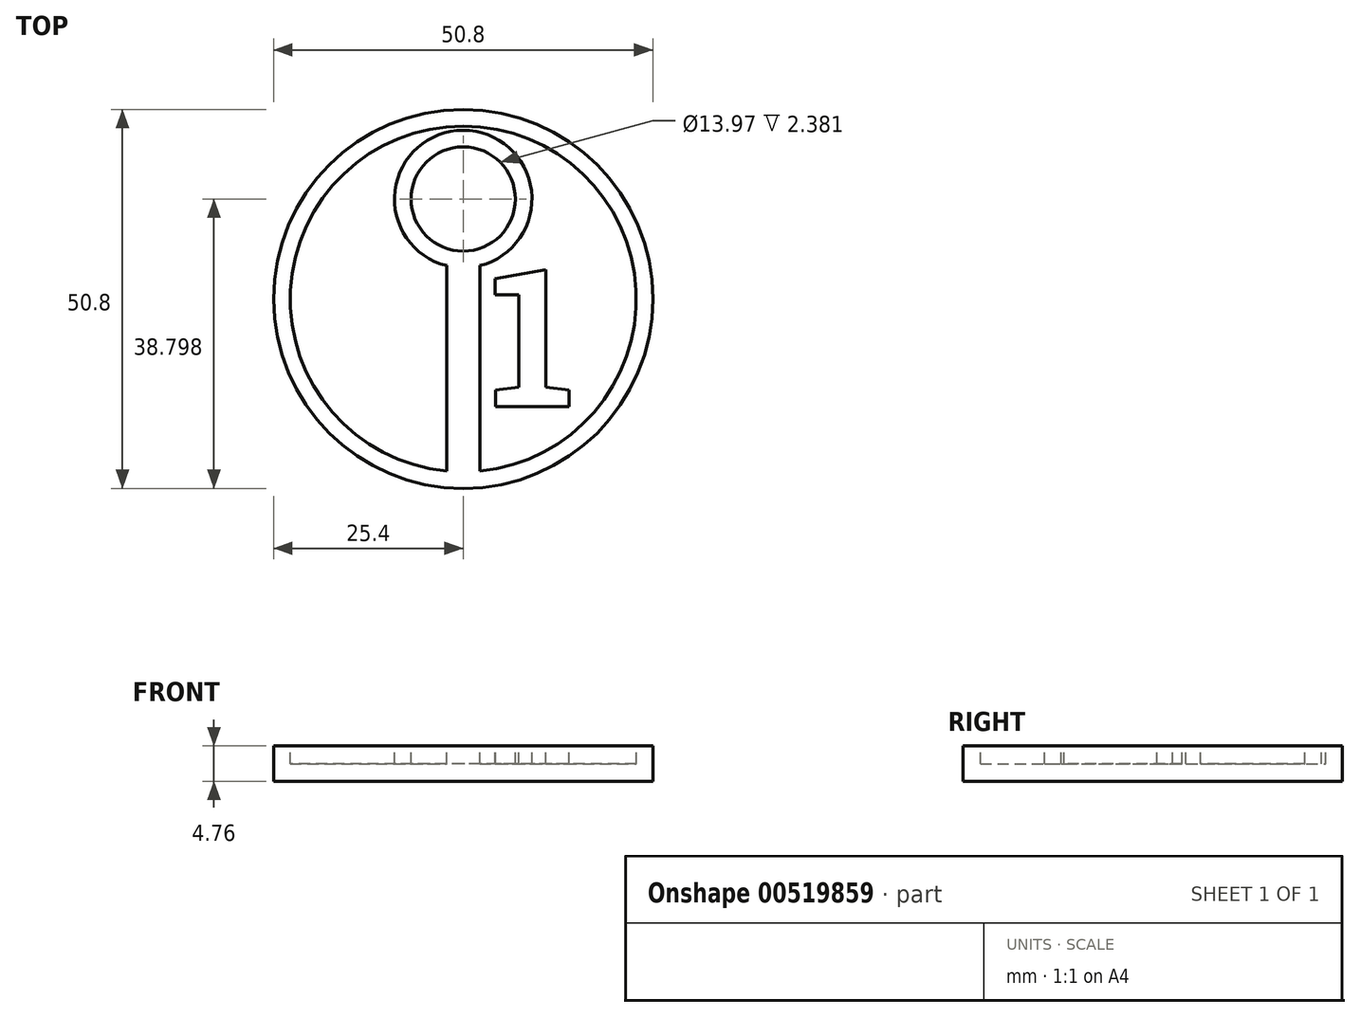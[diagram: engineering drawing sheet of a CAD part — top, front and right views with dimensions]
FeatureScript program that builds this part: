
annotation { "Feature Type Name" : "Feature", "Feature Type Description" : "" }
export const myFeature = defineFeature(function(context is Context, id is Id, definition is map)
    precondition{}
    {
        {
            var Q0;
            Q0=qCreatedBy(makeId("Top.planeOp"),FACE);
            var sketch = newSketch(context, id + "F0", { "sketchPlane" : qUnion([Q0])});
            skCircle(sketch, "E0", {"center": v(0, 0) * mm, "radius": 25.4 * mm});
            skSolve(sketch);
        }
        {
            var Q0;
            Q0 = qSketchRegion(id + "F0", true);
            extrude(context, id + "F1", {"entities" : qUnion([Q0]), "depth" : 4.76 * mm, "offsetDistance" : 25.4 * mm});
        }
        {
            var Q0;
            Q0=makeQuery(id+"F1.opExtrude","CAP_FACE",FACE,{"disambiguationData":[OSD([sQuery(id+"F0.wireOp",EDGE,"E0")])],"isStart":false});
            var sketch = newSketch(context, id + "F2", { "sketchPlane" : qUnion([Q0])});
            skCircle(sketch, "E1", {"center": v(0, 0) * mm, "radius": 23.18 * mm});
            skCircle(sketch, "E2", {"center": v(0, 13.4) * mm, "radius": 6.99 * mm});
            skLineSegment(sketch, "E3.0", {"start": v(2.22, -23.07) * mm, "end": v(2.22, 4.46) * mm});
            skLineSegment(sketch, "E4", {"start": v(-2.22, 4.46) * mm, "end": v(-2.22, -23.07) * mm});
            skArc(sketch, "E5", {"start": v(2.22, 4.46) * mm, "mid": v(0, 22.6) * mm, "end": v(-2.22, 4.46) * mm});
            skSolve(sketch);
        }
        {
            var Q0;
            {var subQ0=sQuery(id+"F2.wireOp",EDGE,"E3.0");Q0=makeQuery(id+"F2.imprint","IMPRINT",FACE,{"disambiguationData":[TD([[makeQuery(id+"F2.imprint","IMPRINT",EDGE,{"derivedFrom":subQ0}),-1.0]])]});}
            extrude(context, id + "F3", {"entities" : qUnion([Q0]), "operationType" : NewBodyOperationType.REMOVE, "oppositeDirection" : true, "depth" : 2.38 * mm, "offsetDistance" : 25.4 * mm});
        }
        {
            var Q0;
            Q0=makeQuery(id+"F2.imprint","IMPRINT",FACE,{"disambiguationData":[TD([[makeQuery(id+"F2.imprint","IMPRINT",EDGE,{"derivedFrom":sQuery(id+"F2.wireOp",EDGE,"E2")}),1.0]])]});
            extrude(context, id + "F4", {"entities" : qUnion([Q0]), "operationType" : NewBodyOperationType.REMOVE, "oppositeDirection" : true, "depth" : 2.38 * mm, "offsetDistance" : 25.4 * mm});
        }
        {
            var Q0;
            {var subQ0=sQuery(id+"F2.wireOp",EDGE,"E3.0");Q0=makeQuery(id+"F2.imprint","IMPRINT",FACE,{"disambiguationData":[TD([[makeQuery(id+"F2.imprint","IMPRINT",EDGE,{"derivedFrom":subQ0}),-1.0]])]});}
            var sketch = newSketch(context, id + "F5", { "sketchPlane" : qUnion([Q0])});
            skPoint(sketch, "E6", {"position": v(3.5, 4.16) * mm});
            skPoint(sketch, "E7", {"position": v(15.77, -14.44) * mm});
            skText(sketch, "E8", { "text": "1", "fontName": "RobotoSlab-Bold.ttf"});
            const initialGuessF5  = {"E8": [0.0035, -0.01444, 1, 0, 0.0186]};
            skSetInitialGuess(sketch, initialGuessF5);
            skSolve(sketch);
        }
        {
            var Q0;
            Q0 = qSketchRegion(id + "F5", true);
            extrude(context, id + "F6", {"entities" : qUnion([Q0]), "operationType" : NewBodyOperationType.ADD, "oppositeDirection" : true, "depth" : 2.38 * mm, "offsetDistance" : 25.4 * mm});
        }
    });
